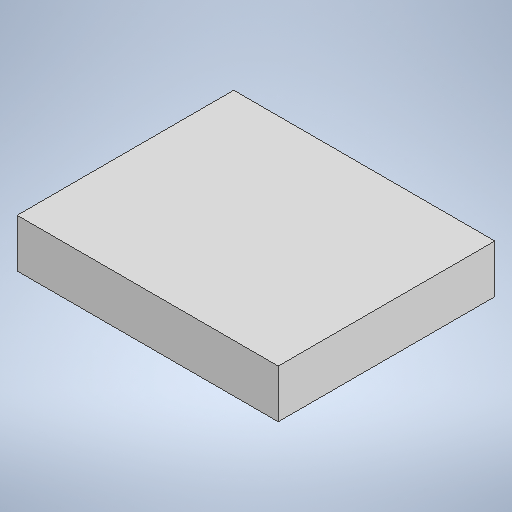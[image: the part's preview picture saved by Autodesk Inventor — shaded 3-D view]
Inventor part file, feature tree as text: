
AUTODESK INVENTOR PART (.ipt)
format: ipt  version: 2025.1 (Build 291241000, 241)  size: 223,744 bytes
history: native  units: mm
features: extrude x3, sketch x3
ambient origin geometry x8: Origin, YZ Plane, XZ Plane, XY Plane, X Axis, Y Axis, Z Axis, Center Point
bodies: Solide1 (feature_tree)
feature tree (6):
  extrude  "Extrusion1"  Depth=176.0mm
  extrude  "Extrusion2"  Depth=146.0mm
  extrude  "Extrusion3"  Depth=2.0mm TaperAngle=0.0deg
  sketch  "Esquisse1"
  sketch  "Esquisse3"
  sketch  "Esquisse4"
